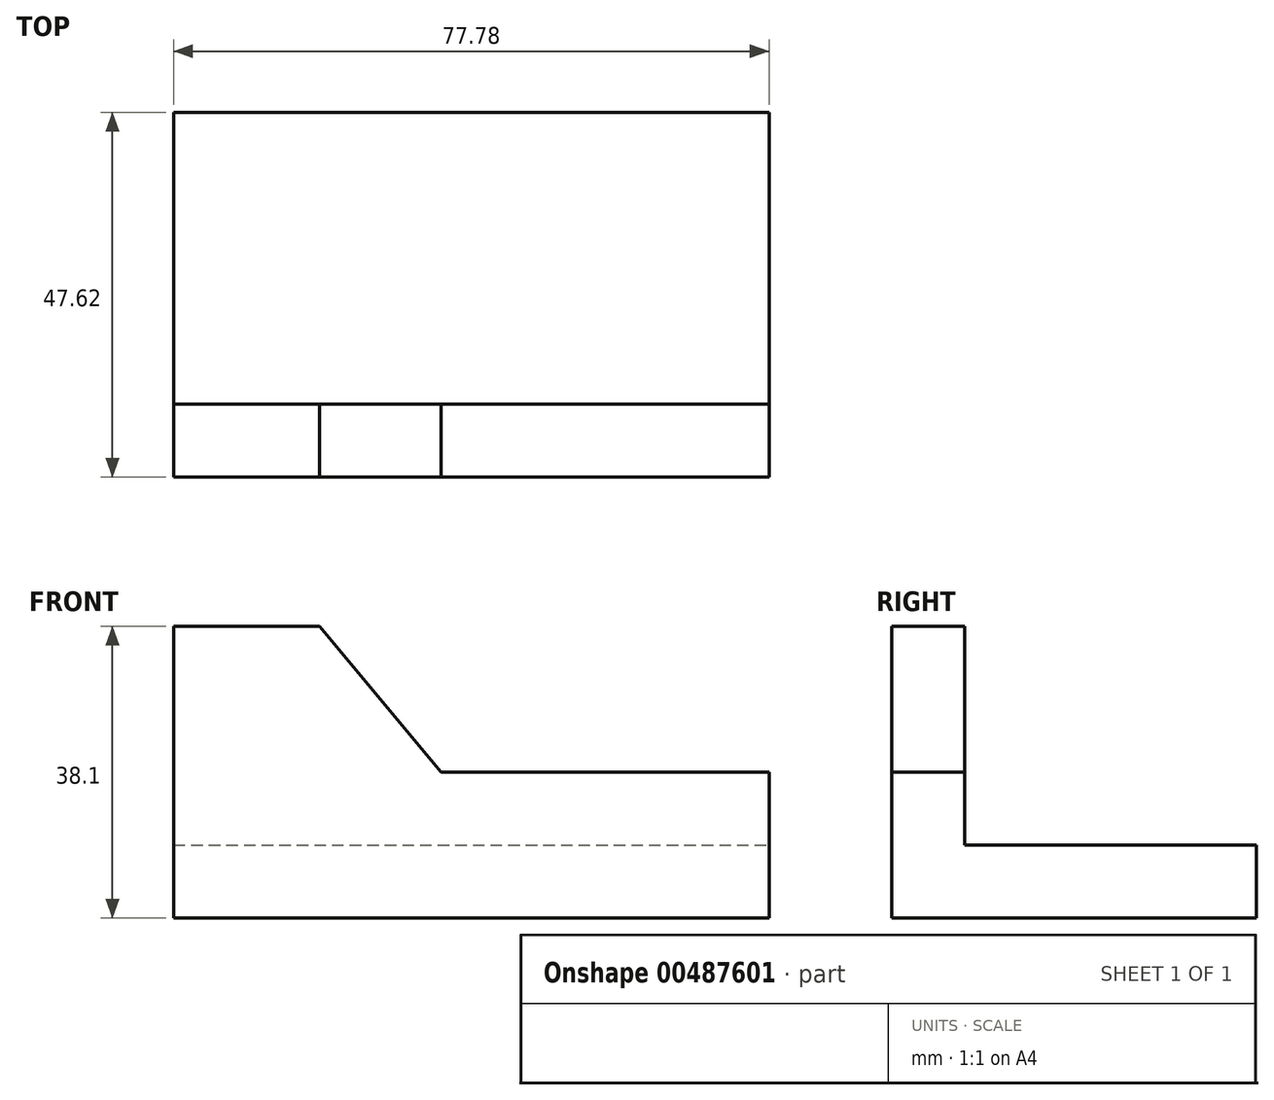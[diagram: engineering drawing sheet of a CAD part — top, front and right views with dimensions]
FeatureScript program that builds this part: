
annotation { "Feature Type Name" : "Feature", "Feature Type Description" : "" }
export const myFeature = defineFeature(function(context is Context, id is Id, definition is map)
    precondition{}
    {
        {
            var Q0;
            Q0=qCreatedBy(makeId("Top.planeOp"),FACE);
            var sketch = newSketch(context, id + "F0", { "sketchPlane" : qUnion([Q0])});
            skLineSegment(sketch, "E0.bottom", {"start": v(-38.9, -23.81) * mm, "end": v(38.9, -23.81) * mm});
            skLineSegment(sketch, "E0.top", {"start": v(-38.9, 23.81) * mm, "end": v(38.9, 23.81) * mm});
            skLineSegment(sketch, "E0.left", {"start": v(-38.9, -23.81) * mm, "end": v(-38.9, 23.81) * mm});
            skLineSegment(sketch, "E0.right", {"start": v(38.9, -23.81) * mm, "end": v(38.9, 23.81) * mm});
            skPoint(sketch, "E0.middle", {"position": v(0, 0) * mm});
            skSolve(sketch);
        }
        {
            var Q0;
            Q0=makeQuery(id+"F0.imprint","IMPRINT",FACE,{"disambiguationData":[TD([[makeQuery(id+"F0.imprint","IMPRINT",EDGE,{"derivedFrom":sQuery(id+"F0.wireOp",EDGE,"E0.bottom")}),1.0]])]});
            extrude(context, id + "F1", {"entities" : qUnion([Q0]), "depth" : 9.52 * mm});
        }
        {
            var Q0;
            Q0=makeQuery(id+"F1.opExtrude","SWEPT_FACE",FACE,{"disambiguationData":[OSD([sQuery(id+"F0.wireOp",EDGE,"E0.bottom")])]});
            var sketch = newSketch(context, id + "F2", { "sketchPlane" : qUnion([Q0])});
            skLineSegment(sketch, "E1", {"start": v(-38.9, 0) * mm, "end": v(-38.9, 38.1) * mm});
            skLineSegment(sketch, "E2", {"start": v(-38.9, 38.1) * mm, "end": v(-19.84, 38.1) * mm});
            skLineSegment(sketch, "E3", {"start": v(-19.84, 38.1) * mm, "end": v(-3.97, 19.05) * mm});
            skLineSegment(sketch, "E4", {"start": v(-3.97, 19.05) * mm, "end": v(38.9, 19.05) * mm});
            skLineSegment(sketch, "E5", {"start": v(38.9, 19.05) * mm, "end": v(38.9, 0) * mm});
            skLineSegment(sketch, "E6", {"start": v(38.9, 0) * mm, "end": v(-38.9, 0) * mm});
            skSolve(sketch);
        }
        {
            var Q0;
            {var subQ1=sQuery(id+"F2.wireOp",EDGE,"E2");Q0=makeQuery(id+"F2.imprint","IMPRINT",FACE,{"disambiguationData":[TD([[makeQuery(id+"F2.imprint","IMPRINT",EDGE,{"derivedFrom":subQ1}),-1.0]])]});}
            extrude(context, id + "F3", {"entities" : qUnion([Q0]), "operationType" : NewBodyOperationType.ADD, "oppositeDirection" : true, "depth" : 9.52 * mm});
        }
    });
